# Revit family: LEGRAND_NON INTERLOCKED SOCKETS_FLUSH MOUNTED_IP66_440
name_source: partatom
category: Installations électriques
revit_build: Autodesk Revit 2018 (Build: 20170223_1515(x64)
units: mm (PartAtom-declared; Revit-internal decimal feet)

## family parameters
Conserver l'orientation des annotations = Non
Cote de connecteur circulaire = Utiliser le diamètre
Couper avec des vides une fois chargée = Non
Hôte = Face
Partagée = Non
Point de calcul de pièce = Non
Type d'élément = Normal

## types (4) — shared parameters
Description = international standard socket for flush or surface mounting with accessory allows the connection of power devices
Elévation par défaut = 1000 mm  [stored 3.28084 ft]
Fabricant = Legrand
Flush E or Surface mounting S = flush and surface mounting
General Conditions of Use = https://export.legrand.com
Maximum installation temperature = 40°C
Maximum use temperature = 100°C
Minimum installation temperature = -20°C
Minimum use temperature = -50°C
Position of earth h = 11
Standard IEC or NFC = IEC
Tension V = 400 440 V  50 60 Hz red
characteristic color = red
connecting type = screw terminals
halogen free = Non
material of box = plastic
resistance to chocks IK = 09

## per-type parameters (varying)
| type | Dia bouchon | Modèle | Number of poles | RAY BOUCHON | Ray | dIA | depth for flush mounting mm | depth mm | h1 | height mm | horizontal fixing distance mm | intensity A | protection class IP | vertical fixing distance mm | width mm |
| panel mounting socket Hypra  IP66/67-55   16A   440 V   3P+E   plast | 79 mm | 051131 | 4 | 40 mm | 26 mm | 53 mm | 41 mm | 89 mm  [stored 0.291995 ft] | 50 mm | 84 mm | 60 mm | 16 A | IP66/67-55 | 70 mm | 74 mm |
| panel mounting socket Hypra IP44 16A   3P+N+E   440V   plast | 82 mm | 051132 | 5 | 41 mm | 27 mm | 55 mm | 44 mm | 88 mm | 50 mm | 84 mm | 60 mm | 16 A | IP44 | 70 mm | 80 mm |
| panel mounting socket Hypra    IP66/67-55   32A   3P+E   440V   plast | 89 mm  [stored 0.291995 ft] | 058136 | 4 | 45 mm | 30 mm  [stored 0.0984252 ft] | 59 mm | 54 mm | 92 mm | 56 mm | 94 mm | 70 mm | 32 A | IP66/67-55 | 70 mm | 84 mm |
| panel mounting socket Hypra   IP66/67-55   3P+E   63A   440 V plast | 106 mm | 058225 | 4 | 53 mm | 35 mm | 71 mm | 85 mm | 164 mm | 64 mm | 106 mm | 77 mm | 63 A | IP66/67-55 | 85 mm | 106 mm |

note: [stored X ft] marks values corroborated as IEEE doubles in the binary element streams (Revit-internal decimal feet)
